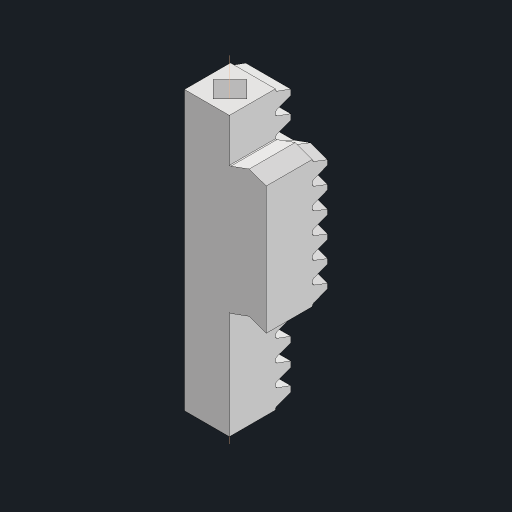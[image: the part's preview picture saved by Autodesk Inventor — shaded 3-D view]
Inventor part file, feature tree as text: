
AUTODESK INVENTOR PART (.ipt)
format: ipt  version: 2023.2 (Build 272271030, 271C)  size: 664,064 bytes
history: native  units: mm
features: sketch x6, projected_geometry x5, extrude x4, sweep x1, pattern_linear x1, other x1
ambient origin geometry x8: Origin, YZ Plane, XZ Plane, XY Plane, X Axis, Y Axis, Z Axis, Center Point
bodies: Solid1 (feature_tree)
feature tree (18):
  extrude  "Extrusion1"  Depth=40.840704mm
  sweep  "Sweep1"
  pattern_linear  "Rectangular Pattern1"  Spacing1=7.0mm  [1 undecoded]
  sketch  "Sketch4"  dims[d6=1.570796mm]
  extrude  "Extrusion7"  Depth=3.5mm
  extrude  "Extrusion8"  Depth=3.5mm
  extrude  "Extrusion9"  TaperAngle=0.0deg  [1 undecoded]
  other  "Work Axis1"
  sketch  "Sketch1"  dims[d0=12.0mm d1=40.840704mm]
  sketch  "Sketch2"  dims[d2=9.0mm d3=0.0mm d4=1.0mm]
  projected_geometry  "Projected Loop1"
  sketch  "Sketch3"  dims[d5=1.25mm]
  projected_geometry  "Projected Loop2"
  sketch  "Sketch8"  dims[d7=12.217305mm]
  projected_geometry  "Projected Loop21"
  sketch  "Sketch9"  dims[d17=0.38mm d27=7.0mm d28=5.0mm d29=3.490659mm d30=0.0mm d31=0.0mm d32=140.0mm d34=3.141593mm d49=10.0mm d50=0.0mm d56=0.0mm d57=0.0mm d58=0.0mm d59=0.0mm d60=3.5mm d61=3.3mm d43=0.5mm d44=0.872665mm d45=0.5mm d46=0.872665mm]
  projected_geometry  "Projected Loop22"
  projected_geometry  "Projected Loop23"
note: 2 required parameter values undecoded (feature->parameter linkage not recoverable at this tier; creation-order binding heuristic only, values carry confidence <= 0.55)
